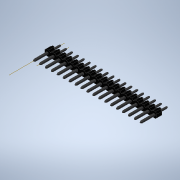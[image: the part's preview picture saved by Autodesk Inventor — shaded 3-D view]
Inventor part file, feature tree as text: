
AUTODESK INVENTOR PART (.ipt)
format: ipt  version: 2020 (Build 240168000, 168)  size: 568,832 bytes
history: native  units: in
note: dims shown in document units (in); Inventor stores cm internally (conversion verified against a paired STEP export)
features: plane x3, other x2, imported_body x1
ambient origin geometry x8: Origin, YZ Plane, XZ Plane, XY Plane, X Axis, Y Axis, Z Axis, Center Point
bodies: Solid1 (feature_tree)
feature tree (6):
  plane  "Work Plane1"
  plane  "Work Plane2"
  plane  "Work Plane3"
  other  "Work Axis1"
  other  "Work Axis2"
  imported_body  "Imported1"
